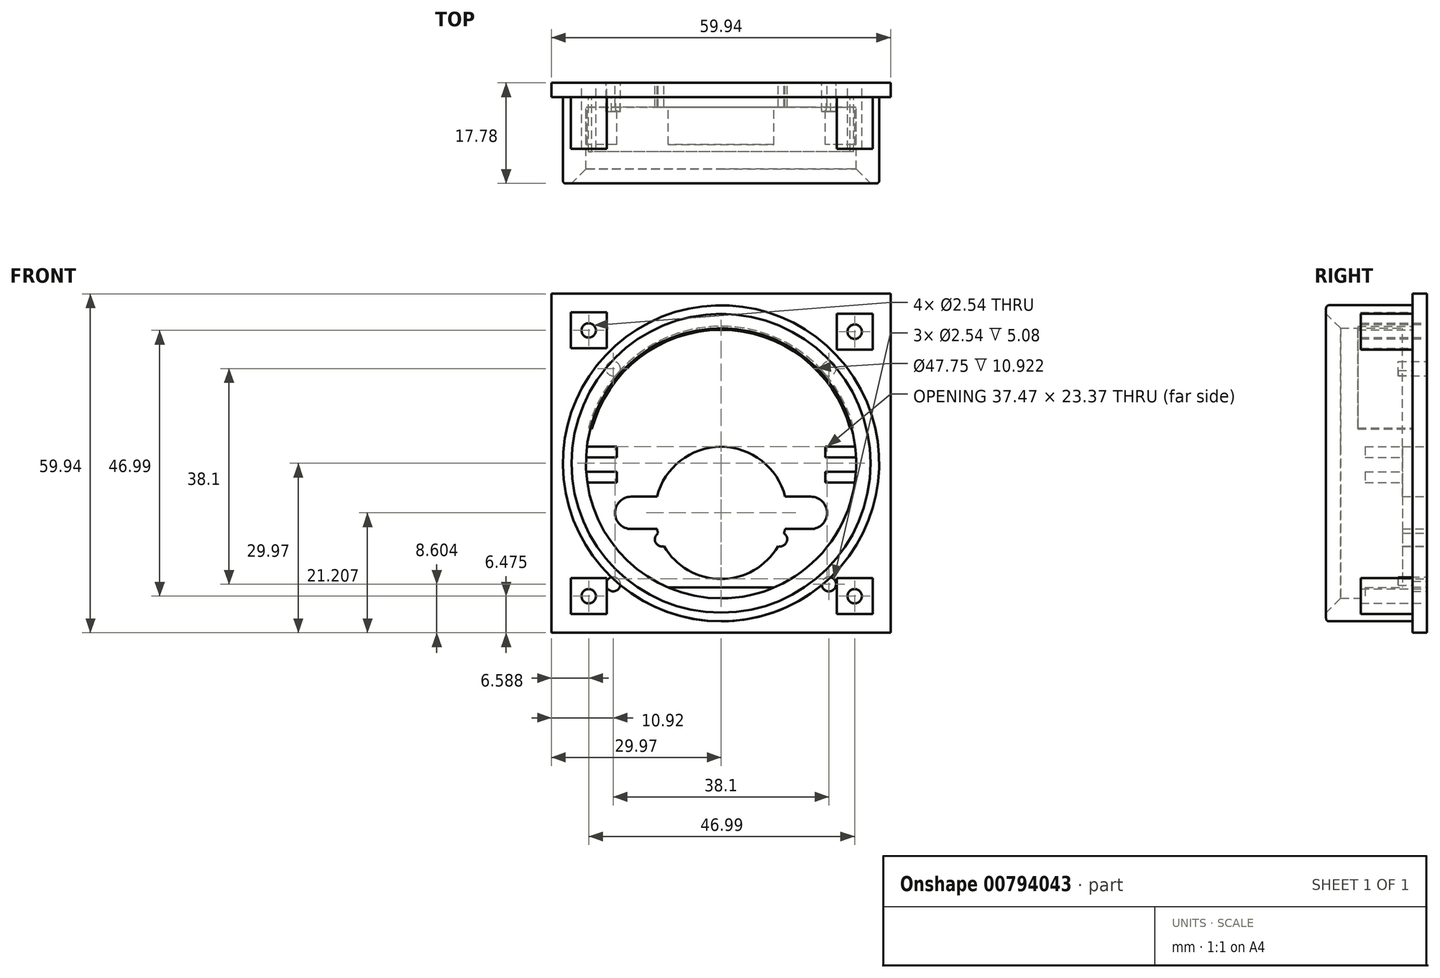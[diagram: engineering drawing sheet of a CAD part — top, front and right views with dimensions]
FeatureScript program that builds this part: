
annotation { "Feature Type Name" : "Feature", "Feature Type Description" : "" }
export const myFeature = defineFeature(function(context is Context, id is Id, definition is map)
    precondition{}
    {
        {
            var Q0;
            Q0=qCreatedBy(makeId("Front.planeOp"),FACE);
            var sketch = newSketch(context, id + "F0", { "sketchPlane" : qUnion([Q0])});
            skCircle(sketch, "E0", {"center": v(0, 0) * mm, "radius": 24.26 * mm});
            skCircle(sketch, "E1", {"center": v(0, -8.76) * mm, "radius": 11.68 * mm});
            skCircle(sketch, "E2", {"center": v(-15.88, -8.76) * mm, "radius": 2.86 * mm});
            skCircle(sketch, "E3", {"center": v(15.88, -8.76) * mm, "radius": 2.86 * mm});
            skPoint(sketch, "E4", {"position": v(-10.41, -13.44) * mm});
            skPoint(sketch, "E5", {"position": v(10.41, -13.44) * mm});
            skLineSegment(sketch, "E6.bottom", {"start": v(15.87, -5.9) * mm, "end": v(-15.88, -5.9) * mm});
            skLineSegment(sketch, "E6.top", {"start": v(15.88, -11.62) * mm, "end": v(-15.88, -11.62) * mm});
            skLineSegment(sketch, "E6.left", {"start": v(15.88, -5.9) * mm, "end": v(15.88, -11.62) * mm});
            skLineSegment(sketch, "E6.right", {"start": v(-15.88, -5.9) * mm, "end": v(-15.88, -11.62) * mm});
            skLineSegment(sketch, "E7.bottom", {"start": v(29.97, 29.97) * mm, "end": v(-29.97, 29.97) * mm});
            skLineSegment(sketch, "E7.top", {"start": v(29.97, -29.97) * mm, "end": v(-29.97, -29.97) * mm});
            skLineSegment(sketch, "E7.left", {"start": v(29.97, 29.97) * mm, "end": v(29.97, -29.97) * mm});
            skLineSegment(sketch, "E7.right", {"start": v(-29.97, 29.97) * mm, "end": v(-29.97, -29.97) * mm});
            skPoint(sketch, "E8", {"position": v(-23.38, 23.5) * mm});
            skPoint(sketch, "E9", {"position": v(23.6, 23.27) * mm});
            skPoint(sketch, "E10", {"position": v(23.6, -23.5) * mm});
            skPoint(sketch, "E11", {"position": v(-23.38, -23.5) * mm});
            skLineSegment(sketch, "E12.bottom", {"start": v(-20.2, 26.67) * mm, "end": v(-26.56, 26.67) * mm});
            skLineSegment(sketch, "E12.top", {"start": v(-20.2, 20.32) * mm, "end": v(-26.56, 20.32) * mm});
            skLineSegment(sketch, "E12.left", {"start": v(-20.2, 26.67) * mm, "end": v(-20.2, 20.32) * mm});
            skLineSegment(sketch, "E12.right", {"start": v(-26.56, 26.67) * mm, "end": v(-26.56, 20.32) * mm});
            skLineSegment(sketch, "E13.bottom", {"start": v(26.78, 26.44) * mm, "end": v(20.43, 26.44) * mm});
            skLineSegment(sketch, "E13.top", {"start": v(26.78, 20.1) * mm, "end": v(20.43, 20.1) * mm});
            skLineSegment(sketch, "E13.left", {"start": v(26.78, 26.44) * mm, "end": v(26.78, 20.1) * mm});
            skLineSegment(sketch, "E13.right", {"start": v(20.43, 26.44) * mm, "end": v(20.43, 20.1) * mm});
            skLineSegment(sketch, "E14.bottom", {"start": v(26.78, -20.32) * mm, "end": v(20.43, -20.32) * mm});
            skLineSegment(sketch, "E14.top", {"start": v(26.78, -26.67) * mm, "end": v(20.43, -26.67) * mm});
            skLineSegment(sketch, "E14.left", {"start": v(26.78, -20.32) * mm, "end": v(26.78, -26.67) * mm});
            skLineSegment(sketch, "E14.right", {"start": v(20.43, -20.32) * mm, "end": v(20.43, -26.67) * mm});
            skLineSegment(sketch, "E15.bottom", {"start": v(-20.2, -20.32) * mm, "end": v(-26.56, -20.32) * mm});
            skLineSegment(sketch, "E15.top", {"start": v(-20.2, -26.67) * mm, "end": v(-26.56, -26.67) * mm});
            skLineSegment(sketch, "E15.left", {"start": v(-20.2, -20.32) * mm, "end": v(-20.2, -26.67) * mm});
            skLineSegment(sketch, "E15.right", {"start": v(-26.56, -20.32) * mm, "end": v(-26.56, -26.67) * mm});
            skSolve(sketch);
        }
        {
            var Q0;
            Q0=makeQuery(id+"F0.imprint","IMPRINT",FACE,{"disambiguationData":[TD([[makeQuery(id+"F0.imprint","IMPRINT",EDGE,{"derivedFrom":sQuery(id+"F0.wireOp",EDGE,"E0")}),1.0]])]});
            extrude(context, id + "F1", {"entities" : qUnion([Q0]), "depth" : 4.32 * mm, "offsetDistance" : 25.4 * mm});
        }
        {
            var Q0;
            Q0=sQuery(id+"F0.wireOp",VERTEX,"E4");
            var Q1;
            Q1=sQuery(id+"F0.wireOp",VERTEX,"E5");
            var Q2;
            Q2=makeQuery(id+"F1.opExtrude","SWEPT_BODY",BODY,{"disambiguationData":[OSD([sQuery(id+"F0.wireOp",EDGE,"E0"),sQuery(id+"F0.wireOp",EDGE,"E1"),sQuery(id+"F0.wireOp",EDGE,"E2"),sQuery(id+"F0.wireOp",EDGE,"E3"),sQuery(id+"F0.wireOp",EDGE,"AQVEhfqM-bFfV-HZmN-Bbqf-DNwuXJOXuMRX.top"),sQuery(id+"F0.wireOp",EDGE,"FJdyEDiO-yEiY-Ot4F-tMeN-V1f38BCFD4gc.top")])]});
            hole(context, id + "F2", {"style" : HoleStyle.SIMPLE, "endStyle" : HoleEndStyle.THROUGH, "oppositeDirection" : true, "holeDiameter" : 2.54 * mm, "majorDiameter" : 6.35 * mm, "isTappedThrough" : true, "tappedDepth" : 12.7 * mm, "tapClearance" : 3, "locations" : qUnion([Q0, Q1]), "scope" : qUnion([Q2])});
        }
        {
            var Q0;
            {var subQ4=sQuery(id+"F0.wireOp",EDGE,"E6.right");Q0=makeQuery(id+"F0.imprint","IMPRINT",FACE,{"disambiguationData":[TD([[makeQuery(id+"F0.imprint","IMPRINT",EDGE,{"derivedFrom":subQ4}),1.0]])]});}
            var Q1;
            {var subQ0=sQuery(id+"F0.wireOp",EDGE,"E6.right");Q1=makeQuery(id+"F0.imprint","IMPRINT",FACE,{"disambiguationData":[TD([[makeQuery(id+"F0.imprint","IMPRINT",EDGE,{"derivedFrom":subQ0}),-1.0]])]});}
            var Q2;
            {var subQ4=sQuery(id+"F0.wireOp",EDGE,"E6.left");Q2=makeQuery(id+"F0.imprint","IMPRINT",FACE,{"disambiguationData":[TD([[makeQuery(id+"F0.imprint","IMPRINT",EDGE,{"derivedFrom":subQ4}),-1.0]])]});}
            var Q3;
            {var subQ0=sQuery(id+"F0.wireOp",EDGE,"E6.left");Q3=makeQuery(id+"F0.imprint","IMPRINT",FACE,{"disambiguationData":[TD([[makeQuery(id+"F0.imprint","IMPRINT",EDGE,{"derivedFrom":subQ0}),1.0]])]});}
            var Q4;
            {var subQ0=sQuery(id+"F0.wireOp",EDGE,"E6.bottom");var subQ1=sQuery(id+"F0.wireOp",EDGE,"E1");var subQ2=makeQuery(id+"F0.imprint","INTERSECT",VERTEX,{"disambiguationData":[OD(0.0)],"derivedFrom":[subQ1,subQ0]});Q4=makeQuery(id+"F0.imprint","IMPRINT",FACE,{"disambiguationData":[TD([[makeQuery(id+"F0.imprint","IMPRINT",EDGE,{"disambiguationData":[TD([[subQ2,-1.0]])],"derivedFrom":subQ1}),-1.0]])]});}
            var Q5;
            {var subQ0=sQuery(id+"F0.wireOp",EDGE,"E6.bottom");var subQ1=sQuery(id+"F0.wireOp",EDGE,"E1");var subQ2=makeQuery(id+"F0.imprint","INTERSECT",VERTEX,{"disambiguationData":[OD(1.0)],"derivedFrom":[subQ1,subQ0]});Q5=makeQuery(id+"F0.imprint","IMPRINT",FACE,{"disambiguationData":[TD([[makeQuery(id+"F0.imprint","IMPRINT",EDGE,{"disambiguationData":[TD([[subQ2,1.0]])],"derivedFrom":subQ1}),-1.0]])]});}
            extrude(context, id + "F3", {"entities" : qUnion([Q0, Q1, Q2, Q3, Q4, Q5]), "operationType" : NewBodyOperationType.REMOVE, "oppositeDirection" : true, "depth" : 10.92 * mm, "offsetDistance" : 25.4 * mm});
        }
        {
            var Q0;
            Q0=qCreatedBy(makeId("Front.planeOp"),FACE);
            var sketch = newSketch(context, id + "F4", { "sketchPlane" : qUnion([Q0])});
            skCircle(sketch, "E16", {"center": v(0, 0) * mm, "radius": 23.88 * mm});
            skCircle(sketch, "E17", {"center": v(0, 0) * mm, "radius": 27.94 * mm});
            skSolve(sketch);
        }
        {
            var Q0;
            Q0=qSketchRegion(id+"F4",true);
            extrude(context, id + "F5", {"entities" : qUnion([Q0]), "operationType" : NewBodyOperationType.ADD, "depth" : 17.78 * mm, "offsetDistance" : 25.4 * mm});
        }
        {
            var Q0;
            Q0=qCreatedBy(makeId("Front.planeOp"),FACE);
            cPlane(context, id + "F6", {"entities" : qUnion([Q0]), "cplaneType" : CPlaneType.OFFSET, "offset" : 2.54 * mm, "width" : 152.4 * mm, "height" : 152.4 * mm});
        }
        {
            var Q0;
            Q0=qCreatedBy(id+"F6.planeOp",FACE);
            var sketch = newSketch(context, id + "F7", { "sketchPlane" : qUnion([Q0])});
            skLineSegment(sketch, "E18.bottom", {"start": v(12.7, -21.97) * mm, "end": v(-12.7, -21.97) * mm});
            skLineSegment(sketch, "E18.top", {"start": v(12.7, -24.51) * mm, "end": v(-12.7, -24.51) * mm});
            skLineSegment(sketch, "E18.left", {"start": v(12.7, -21.97) * mm, "end": v(12.7, -24.51) * mm});
            skLineSegment(sketch, "E18.right", {"start": v(-12.7, -21.97) * mm, "end": v(-12.7, -24.51) * mm});
            skPoint(sketch, "E18.middle", {"position": v(0, -23.24) * mm});
            skLineSegment(sketch, "E19.bottom", {"start": v(-18.41, 2.92) * mm, "end": v(-24.77, 2.92) * mm});
            skLineSegment(sketch, "E19.top", {"start": v(-18.41, -3.43) * mm, "end": v(-24.77, -3.43) * mm});
            skLineSegment(sketch, "E19.left", {"start": v(-18.41, 2.92) * mm, "end": v(-18.41, -3.43) * mm});
            skLineSegment(sketch, "E19.right", {"start": v(-24.77, 2.92) * mm, "end": v(-24.77, -3.43) * mm});
            skPoint(sketch, "E19.middle", {"position": v(-21.59, -0.25) * mm});
            skLineSegment(sketch, "E20.bottom", {"start": v(24.77, -3.43) * mm, "end": v(18.41, -3.43) * mm});
            skLineSegment(sketch, "E20.top", {"start": v(24.77, 2.92) * mm, "end": v(18.41, 2.92) * mm});
            skLineSegment(sketch, "E20.left", {"start": v(24.77, -3.43) * mm, "end": v(24.77, 2.92) * mm});
            skLineSegment(sketch, "E20.right", {"start": v(18.41, -3.43) * mm, "end": v(18.41, 2.92) * mm});
            skPoint(sketch, "E20.middle", {"position": v(21.59, -0.25) * mm});
            skLineSegment(sketch, "E21.bottom", {"start": v(-18.41, 1.02) * mm, "end": v(-24.76, 1.02) * mm});
            skLineSegment(sketch, "E21.top", {"start": v(-18.41, -1.52) * mm, "end": v(-24.76, -1.52) * mm});
            skLineSegment(sketch, "E21.left", {"start": v(-18.41, 1.02) * mm, "end": v(-18.41, -1.52) * mm});
            skLineSegment(sketch, "E21.right", {"start": v(-24.76, 1.02) * mm, "end": v(-24.76, -1.52) * mm});
            skLineSegment(sketch, "E22.bottom", {"start": v(24.77, 1.02) * mm, "end": v(18.41, 1.02) * mm});
            skLineSegment(sketch, "E22.top", {"start": v(24.77, -1.52) * mm, "end": v(18.41, -1.52) * mm});
            skLineSegment(sketch, "E22.left", {"start": v(24.77, 1.02) * mm, "end": v(24.77, -1.52) * mm});
            skLineSegment(sketch, "E22.right", {"start": v(18.41, 1.02) * mm, "end": v(18.41, -1.52) * mm});
            skSolve(sketch);
        }
        {
            var Q0;
            Q0=makeQuery(id+"F0.imprint","IMPRINT",FACE,{"disambiguationData":[TD([[makeQuery(id+"F0.imprint","IMPRINT",EDGE,{"derivedFrom":sQuery(id+"F0.wireOp",EDGE,"E0")}),-1.0]])]});
            extrude(context, id + "F8", {"entities" : qUnion([Q0]), "operationType" : NewBodyOperationType.ADD, "depth" : 2.54 * mm, "offsetDistance" : 25.4 * mm});
        }
        {
            var Q0;
            Q0=qCreatedBy(id+"F6.planeOp",FACE);
            var sketch = newSketch(context, id + "F9", { "sketchPlane" : qUnion([Q0])});
            skArc(sketch, "E23", {"start": v(24.26, 0) * mm, "mid": v(0, 24.23) * mm, "end": v(-24.26, 0) * mm});
            skArc(sketch, "E24", {"start": v(23.62, 0) * mm, "mid": v(0, 23.6) * mm, "end": v(-23.62, 0) * mm});
            skLineSegment(sketch, "E25", {"start": v(-23.44, 6.23) * mm, "end": v(-22.83, 6.03) * mm});
            skLineSegment(sketch, "E26", {"start": v(23.43, 6.25) * mm, "end": v(22.8, 6.11) * mm});
            skSolve(sketch);
        }
        {
            var Q0;
            Q0=makeQuery(id+"F9.imprint","IMPRINT",FACE,{"disambiguationData":[TD([[makeQuery(id+"F9.imprint","IMPRINT",EDGE,{"derivedFrom":sQuery(id+"F9.wireOp",EDGE,"E23")}),1.0]])]});
            extrude(context, id + "F10", {"entities" : qUnion([Q0]), "depth" : 9.65 * mm, "offsetDistance" : 25.4 * mm});
        }
        {
            var Q0;
            Q0=qCreatedBy(makeId("Front.planeOp"),FACE);
            var sketch = newSketch(context, id + "F11", { "sketchPlane" : qUnion([Q0])});
            skCircle(sketch, "E27", {"center": v(19.05, 16.73) * mm, "radius": 1.27 * mm});
            skCircle(sketch, "E28", {"center": v(-19.05, 16.73) * mm, "radius": 1.27 * mm});
            skCircle(sketch, "E29", {"center": v(-19.05, -21.37) * mm, "radius": 1.27 * mm});
            skCircle(sketch, "E30", {"center": v(19.05, -21.37) * mm, "radius": 1.27 * mm});
            skSolve(sketch);
        }
        {
            var Q0;
            Q0=makeQuery(id+"F11.imprint","IMPRINT",FACE,{"disambiguationData":[TD([[makeQuery(id+"F11.imprint","IMPRINT",EDGE,{"derivedFrom":sQuery(id+"F11.wireOp",EDGE,"E27")}),1.0]])]});
            var Q1;
            Q1=makeQuery(id+"F11.imprint","IMPRINT",FACE,{"disambiguationData":[TD([[makeQuery(id+"F11.imprint","IMPRINT",EDGE,{"derivedFrom":sQuery(id+"F11.wireOp",EDGE,"E28")}),1.0]])]});
            var Q2;
            Q2=makeQuery(id+"F11.imprint","IMPRINT",FACE,{"disambiguationData":[TD([[makeQuery(id+"F11.imprint","IMPRINT",EDGE,{"derivedFrom":sQuery(id+"F11.wireOp",EDGE,"E29")}),1.0]])]});
            var Q3;
            Q3=makeQuery(id+"F11.imprint","IMPRINT",FACE,{"disambiguationData":[TD([[makeQuery(id+"F11.imprint","IMPRINT",EDGE,{"derivedFrom":sQuery(id+"F11.wireOp",EDGE,"E30")}),1.0]])]});
            extrude(context, id + "F12", {"entities" : qUnion([Q0, Q1, Q2, Q3]), "operationType" : NewBodyOperationType.REMOVE, "depth" : 5.08 * mm, "offsetDistance" : 25.4 * mm});
        }
        {
            var Q0;
            Q0=makeQuery(id+"F7.imprint","IMPRINT",FACE,{"disambiguationData":[TD([[makeQuery(id+"F7.imprint","IMPRINT",EDGE,{"derivedFrom":sQuery(id+"F7.wireOp",EDGE,"E18.bottom")}),1.0]])]});
            var Q1;
            {var subQ0=sQuery(id+"F7.wireOp",EDGE,"E19.bottom");Q1=makeQuery(id+"F7.imprint","IMPRINT",FACE,{"disambiguationData":[TD([[makeQuery(id+"F7.imprint","IMPRINT",EDGE,{"derivedFrom":subQ0}),1.0]])]});}
            var Q2;
            {var subQ0=sQuery(id+"F7.wireOp",EDGE,"E19.top");Q2=makeQuery(id+"F7.imprint","IMPRINT",FACE,{"disambiguationData":[TD([[makeQuery(id+"F7.imprint","IMPRINT",EDGE,{"derivedFrom":subQ0}),-1.0]])]});}
            var Q3;
            {var subQ0=sQuery(id+"F7.wireOp",EDGE,"E20.bottom");Q3=makeQuery(id+"F7.imprint","IMPRINT",FACE,{"disambiguationData":[TD([[makeQuery(id+"F7.imprint","IMPRINT",EDGE,{"derivedFrom":subQ0}),-1.0]])]});}
            var Q4;
            {var subQ0=sQuery(id+"F7.wireOp",EDGE,"E20.top");Q4=makeQuery(id+"F7.imprint","IMPRINT",FACE,{"disambiguationData":[TD([[makeQuery(id+"F7.imprint","IMPRINT",EDGE,{"derivedFrom":subQ0}),1.0]])]});}
            extrude(context, id + "F13", {"entities" : qUnion([Q0, Q1, Q2, Q3, Q4]), "operationType" : NewBodyOperationType.ADD, "depth" : 8.38 * mm, "offsetDistance" : 25.4 * mm});
        }
        {
            var Q0;
            Q0=makeQuery(id+"F0.imprint","IMPRINT",FACE,{"disambiguationData":[TD([[makeQuery(id+"F0.imprint","IMPRINT",EDGE,{"derivedFrom":sQuery(id+"F0.wireOp",EDGE,"E15.bottom")}),1.0]])]});
            var Q1;
            Q1=makeQuery(id+"F0.imprint","IMPRINT",FACE,{"disambiguationData":[TD([[makeQuery(id+"F0.imprint","IMPRINT",EDGE,{"derivedFrom":sQuery(id+"F0.wireOp",EDGE,"E12.bottom")}),1.0]])]});
            var Q2;
            Q2=makeQuery(id+"F0.imprint","IMPRINT",FACE,{"disambiguationData":[TD([[makeQuery(id+"F0.imprint","IMPRINT",EDGE,{"derivedFrom":sQuery(id+"F0.wireOp",EDGE,"E13.bottom")}),1.0]])]});
            var Q3;
            Q3=makeQuery(id+"F0.imprint","IMPRINT",FACE,{"disambiguationData":[TD([[makeQuery(id+"F0.imprint","IMPRINT",EDGE,{"derivedFrom":sQuery(id+"F0.wireOp",EDGE,"E14.bottom")}),1.0]])]});
            extrude(context, id + "F14", {"entities" : qUnion([Q0, Q1, Q2, Q3]), "operationType" : NewBodyOperationType.ADD, "depth" : 11.68 * mm, "offsetDistance" : 25.4 * mm});
        }
        {
            var Q0;
            Q0=sQuery(id+"F0.wireOp",VERTEX,"E8");
            var Q1;
            Q1=sQuery(id+"F0.wireOp",VERTEX,"E9");
            var Q2;
            Q2=sQuery(id+"F0.wireOp",VERTEX,"E11");
            var Q3;
            Q3=sQuery(id+"F0.wireOp",VERTEX,"E10");
            var Q4;
            Q4=makeQuery(id+"F1.opExtrude","SWEPT_BODY",BODY,{"disambiguationData":[OSD([sQuery(id+"F0.wireOp",EDGE,"E0"),sQuery(id+"F0.wireOp",EDGE,"E1"),sQuery(id+"F0.wireOp",EDGE,"E2"),sQuery(id+"F0.wireOp",EDGE,"E3"),sQuery(id+"F0.wireOp",EDGE,"E6.bottom"),sQuery(id+"F0.wireOp",EDGE,"E6.top")])]});
            hole(context, id + "F15", {"style" : HoleStyle.SIMPLE, "endStyle" : HoleEndStyle.THROUGH, "oppositeDirection" : true, "holeDiameter" : 2.54 * mm, "majorDiameter" : 6.35 * mm, "isTappedThrough" : true, "tappedDepth" : 12.7 * mm, "tapClearance" : 3, "locations" : qUnion([Q0, Q1, Q2, Q3]), "scope" : qUnion([Q4])});
        }
        {
            var Q0;
            Q0=makeQuery(id+"F5.opExtrude","CAP_EDGE",EDGE,{"disambiguationData":[OSD([sQuery(id+"F4.wireOp",EDGE,"E16")])],"isStart":false});
            chamfer(context, id + "F16", {"entities" : qUnion([Q0]), "width" : 2.54 * mm, "tangentPropagation" : true});
        }
        {
            var Q0;
            Q0=makeQuery(id+"F5.opExtrude","CAP_EDGE",EDGE,{"disambiguationData":[OSD([sQuery(id+"F4.wireOp",EDGE,"E17")])],"isStart":false});
            fillet(context, id + "F17", {"entities" : qUnion([Q0]), "radius" : 0.5 * mm, "tangentPropagation" : true, "allowEdgeOverflow" : false});
        }
    });
